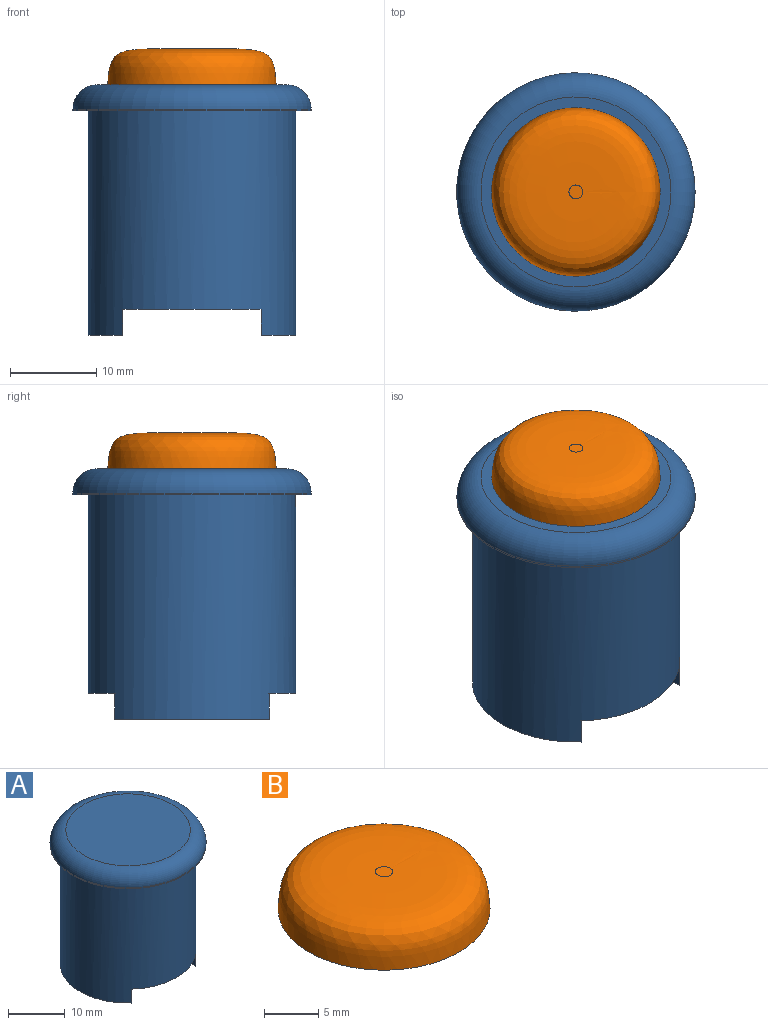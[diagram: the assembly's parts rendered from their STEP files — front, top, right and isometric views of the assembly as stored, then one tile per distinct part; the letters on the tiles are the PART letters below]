
ASSEMBLY  parts=2 mates=1
PART A: 10 faces, bbox 29.9x29.9x29 mm
  f0: plane 17.89x4mm, normal (0,0,-1), area 49.6mm2, adj f1,f9
  f1: cylinder r=12mm len=26mm, axis (0,0,-1), area 1855.3mm2, adj f0,f2,f5,f7,f8,f9
  f2: plane 17.89x4mm, normal (0,0,-1), area 49.6mm2, adj f1,f8
  f3: cylinder r=13.8mm len=27.6mm, axis (0,0,-1), area 17.3mm2, adj f5,f6
  f4: plane 22x22mm, normal (0,0,1), area 380.1mm2, adj f6
  f5: plane 27.6x27.6mm, normal (0,0,-1), area 145.9mm2, adj f1,f3
  f6: torus R=11mm, axis (0,0,1), area 353.2mm2, adj f3,f4
  f7: plane 24x16mm, normal (0,0,-1), area 353.3mm2, adj f1,f8,f9
  f8: plane 17.89x3mm, normal (-1,0,0), area 53.7mm2, adj f1,f2,f7
  f9: plane 17.89x3mm, normal (1,0,0), area 53.7mm2, adj f0,f1,f7
PART B: 3 faces, bbox 20.1x20.1x9 mm
  f0: plane 1.61x1.61mm, normal (0,0,1), area 2mm2, adj f2
  f1: plane 19.53x19.53mm, normal (0,0,-1), area 298.7mm2, adj f2
  f2: bspline ~20.11x20.11mm, area 463.9mm2, adj f0,f1
PLACE A t=(-4.94,-6.62,-5.65)mm
PLACE B t=(-4.94,-6.62,-5.65)mm
MATE fastened B.f1 <-> A.f3  axis (0,0,-1) through (-4.94,-6.62,23.35)mm
